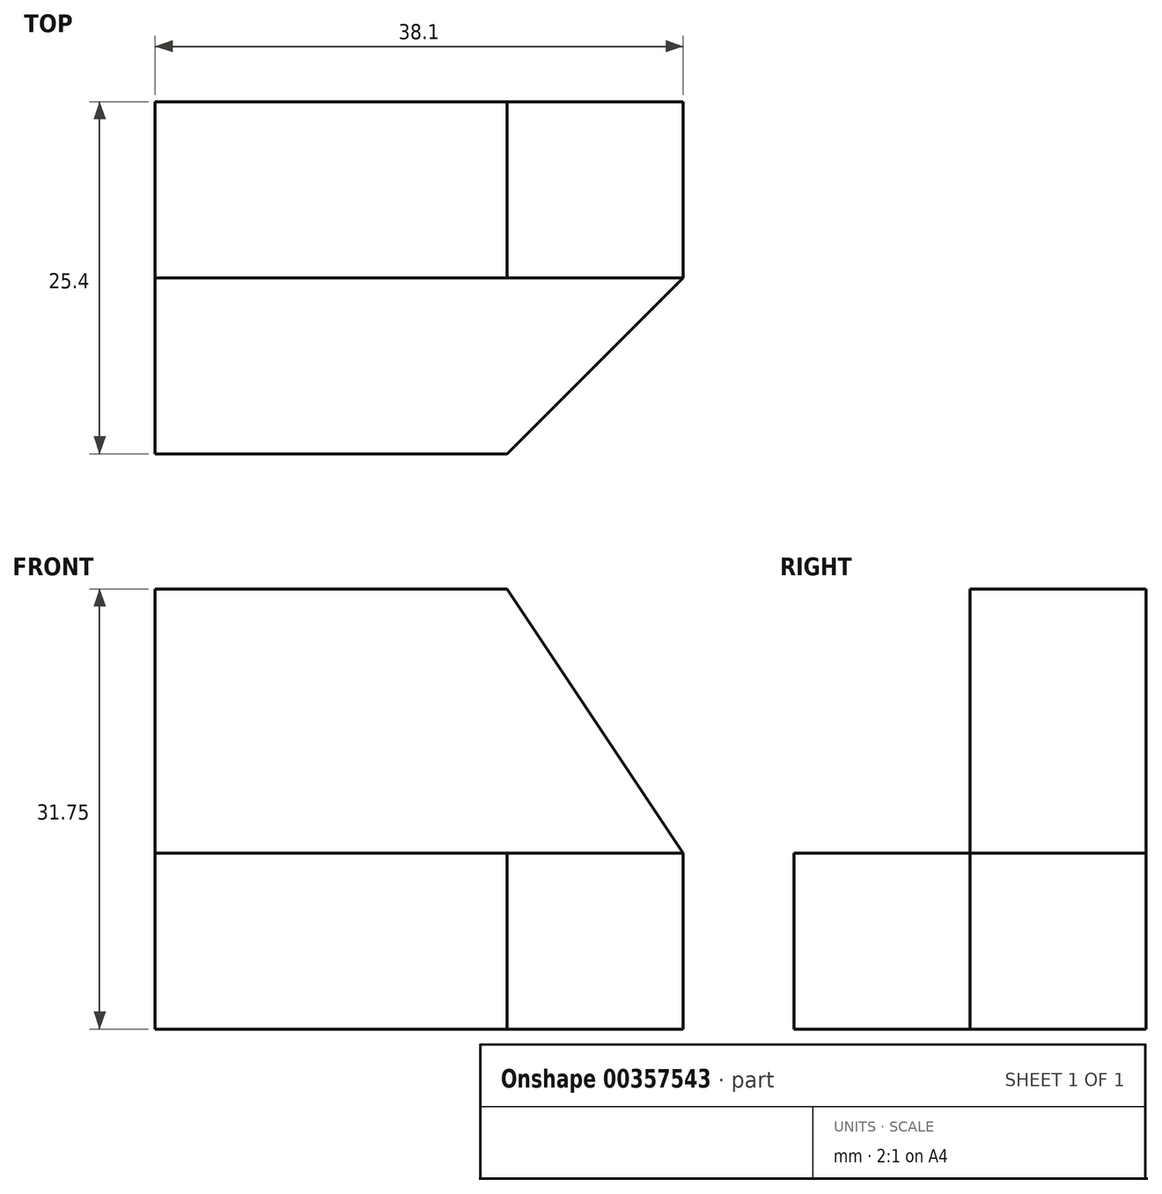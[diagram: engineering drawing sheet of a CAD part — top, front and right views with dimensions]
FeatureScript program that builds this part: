
annotation { "Feature Type Name" : "Feature", "Feature Type Description" : "" }
export const myFeature = defineFeature(function(context is Context, id is Id, definition is map)
    precondition{}
    {
        {
            var Q0;
            Q0=qCreatedBy(makeId("Right.planeOp"),FACE);
            var sketch = newSketch(context, id + "F0", { "sketchPlane" : qUnion([Q0])});
            skLineSegment(sketch, "E0", {"start": v(-54.46, 19.4) * mm, "end": v(-29.06, 19.4) * mm});
            skLineSegment(sketch, "E1", {"start": v(-29.06, 19.4) * mm, "end": v(-29.06, 51.16) * mm});
            skLineSegment(sketch, "E2", {"start": v(-29.06, 51.16) * mm, "end": v(-41.76, 51.16) * mm});
            skLineSegment(sketch, "E3", {"start": v(-41.76, 51.16) * mm, "end": v(-41.76, 32.1) * mm});
            skLineSegment(sketch, "E4", {"start": v(-41.76, 32.1) * mm, "end": v(-54.46, 32.1) * mm});
            skLineSegment(sketch, "E5", {"start": v(-54.46, 32.1) * mm, "end": v(-54.46, 19.4) * mm});
            skSolve(sketch);
        }
        {
            var Q0;
            Q0 = qSketchRegion(id + "F0", true);
            extrude(context, id + "F1", {"entities" : qUnion([Q0]), "depth" : 38.1 * mm});
        }
        {
            var Q0;
            Q0=makeQuery(id+"F1.opExtrude","SWEPT_FACE",FACE,{"disambiguationData":[OSD([sQuery(id+"F0.wireOp",EDGE,"E3")])]});
            var sketch = newSketch(context, id + "F2", { "sketchPlane" : qUnion([Q0])});
            skLineSegment(sketch, "E6", {"start": v(0, 51.16) * mm, "end": v(25.4, 51.16) * mm});
            skLineSegment(sketch, "E7", {"start": v(25.4, 51.16) * mm, "end": v(38.1, 32.1) * mm});
            skLineSegment(sketch, "E8", {"start": v(38.1, 32.1) * mm, "end": v(0, 32.1) * mm});
            skSolve(sketch);
        }
        {
            var Q0;
            {var subQ0=sQuery(id+"F2.wireOp",EDGE,"E7");Q0=makeQuery(id+"F2.imprint","IMPRINT",FACE,{"disambiguationData":[TD([[makeQuery(id+"F2.imprint","IMPRINT",EDGE,{"derivedFrom":subQ0}),1.0]])]});}
            extrude(context, id + "F3", {"entities" : qUnion([Q0]), "operationType" : NewBodyOperationType.REMOVE, "oppositeDirection" : true, "depth" : 12.7 * mm});
        }
        {
            var Q0;
            Q0=makeQuery(id+"F1.opExtrude","SWEPT_FACE",FACE,{"disambiguationData":[OSD([sQuery(id+"F0.wireOp",EDGE,"E4")])]});
            var sketch = newSketch(context, id + "F4", { "sketchPlane" : qUnion([Q0])});
            skLineSegment(sketch, "E9", {"start": v(38.1, -41.76) * mm, "end": v(25.4, -54.46) * mm});
            skLineSegment(sketch, "E10", {"start": v(25.4, -54.46) * mm, "end": v(0, -54.46) * mm});
            skSolve(sketch);
        }
        {
            var Q0;
            {var subQ0=sQuery(id+"F4.wireOp",EDGE,"E9");Q0=makeQuery(id+"F4.imprint","IMPRINT",FACE,{"disambiguationData":[TD([[makeQuery(id+"F4.imprint","IMPRINT",EDGE,{"derivedFrom":subQ0}),1.0]])]});}
            extrude(context, id + "F5", {"entities" : qUnion([Q0]), "operationType" : NewBodyOperationType.REMOVE, "oppositeDirection" : true, "depth" : 12.7 * mm});
        }
    });
